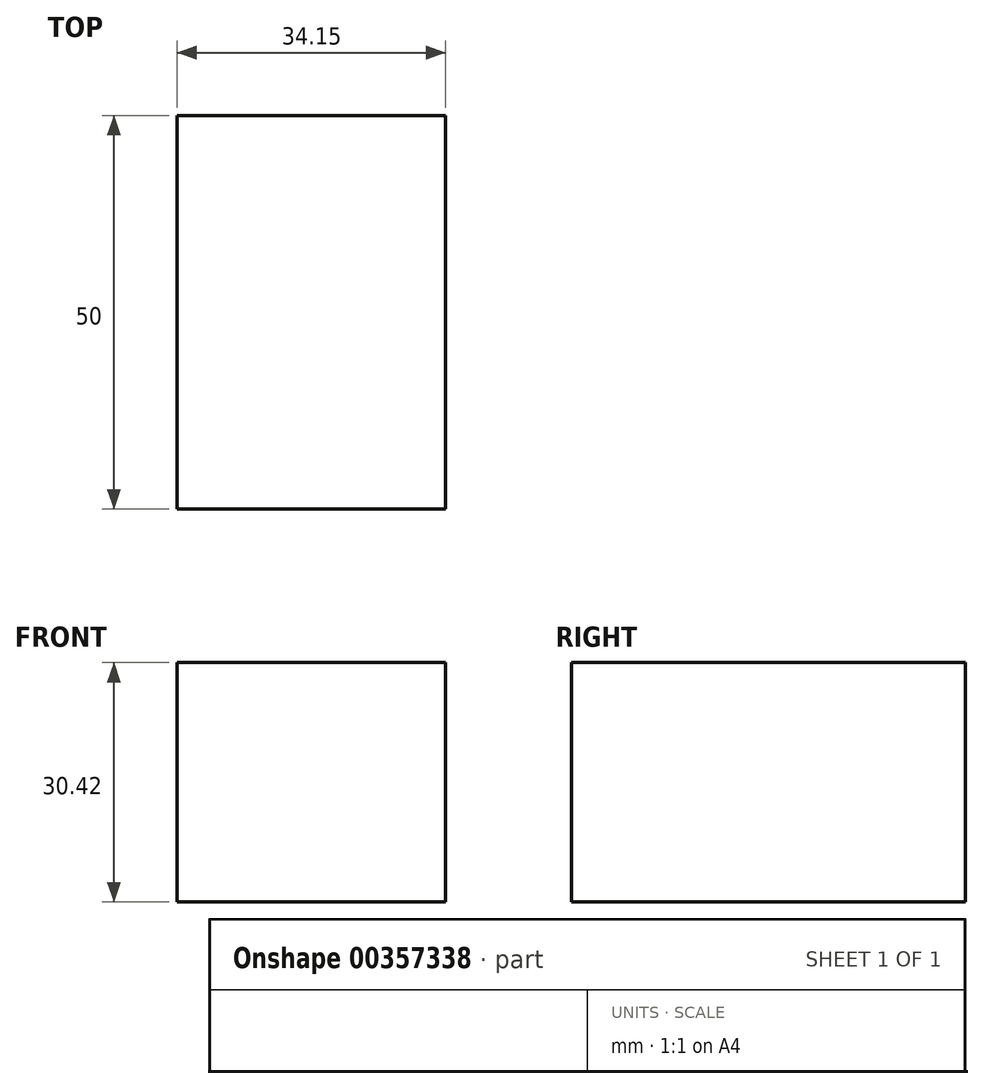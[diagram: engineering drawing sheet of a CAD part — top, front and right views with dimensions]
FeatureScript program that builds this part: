
annotation { "Feature Type Name" : "Feature", "Feature Type Description" : "" }
export const myFeature = defineFeature(function(context is Context, id is Id, definition is map)
    precondition{}
    {
        {
            var Q0;
            Q0=qCreatedBy(makeId("Front.planeOp"),FACE);
            var sketch = newSketch(context, id + "F0", { "sketchPlane" : qUnion([Q0])});
            skLineSegment(sketch, "E0.bottom", {"start": v(0, 0) * mm, "end": v(34.15, 0) * mm});
            skLineSegment(sketch, "E0.top", {"start": v(0, 30.42) * mm, "end": v(34.15, 30.42) * mm});
            skLineSegment(sketch, "E0.left", {"start": v(0, 0) * mm, "end": v(0, 30.42) * mm});
            skLineSegment(sketch, "E0.right", {"start": v(34.15, 0) * mm, "end": v(34.15, 30.42) * mm});
            skSolve(sketch);
        }
        {
            var Q0;
            Q0=makeQuery(id+"F0.imprint","IMPRINT",FACE,{"disambiguationData":[TD([[makeQuery(id+"F0.imprint","IMPRINT",EDGE,{"derivedFrom":sQuery(id+"F0.wireOp",EDGE,"E0.bottom")}),1.0]])]});
            extrude(context, id + "F1", {"entities" : qUnion([Q0]), "depth" : 25 * mm, "hasSecondDirection" : true, "secondDirectionOppositeDirection" : true, "secondDirectionDepth" : 25 * mm});
        }
    });
